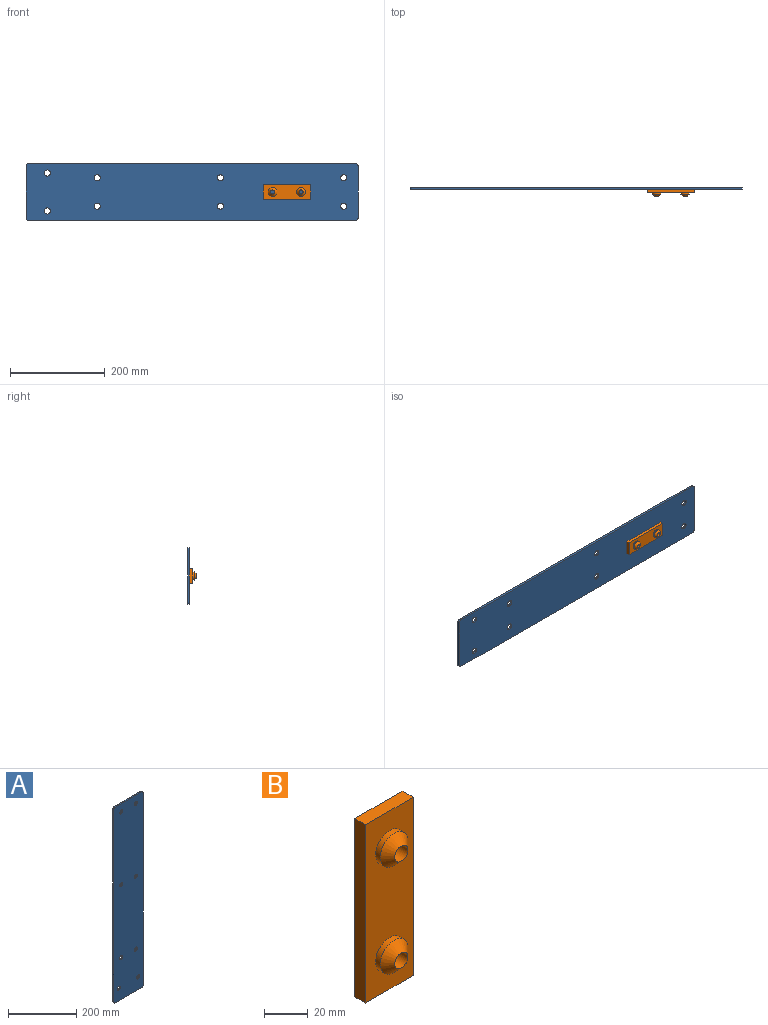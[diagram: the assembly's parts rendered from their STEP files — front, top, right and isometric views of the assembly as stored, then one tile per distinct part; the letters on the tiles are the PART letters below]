
ASSEMBLY  parts=2 mates=1
PART A: 18 faces, bbox 120x4x700 mm
  f0: plane 690x4mm, normal (-1,0,0), area 2760mm2, adj f12,f13,f14,f17
  f1: plane 110x4mm, normal (0,0,-1), area 440mm2, adj f12,f13,f14,f15
  f2: plane 690x4mm, normal (1,0,0), area 2760mm2, adj f12,f13,f15,f16
  f3: cylinder r=6.5mm len=13mm, axis (0,1,0), area 163.4mm2, adj f12,f13
  f4: cylinder r=6.5mm len=13mm, axis (0,1,0), area 163.4mm2, adj f12,f13
  f5: cylinder r=6.5mm len=13mm, axis (0,1,0), area 163.4mm2, adj f12,f13
  f6: cylinder r=6.5mm len=13mm, axis (0,1,0), area 163.4mm2, adj f12,f13
  f7: cylinder r=6.5mm len=13mm, axis (0,1,0), area 163.4mm2, adj f12,f13
  f8: cylinder r=6.5mm len=13mm, axis (0,1,0), area 163.4mm2, adj f12,f13
  f9: cylinder r=6.5mm len=13mm, axis (0,1,0), area 163.4mm2, adj f12,f13
  f10: plane 110x4mm, normal (0,0,1), area 440mm2, adj f12,f13,f16,f17
  f11: cylinder r=6.5mm len=13mm, axis (0,1,0), area 163.4mm2, adj f12,f13
  f12: plane 700x120mm, normal (0,-1,0), area 82916.7mm2, adj f0,f1,f2,f3,f4,f5,f6,f7
  f13: plane 700x120mm, normal (0,1,0), area 82916.7mm2, adj f0,f1,f2,f3,f4,f5,f6,f7
  f14: cylinder r=5mm len=5mm, axis (0,1,0), area 31.4mm2, adj f0,f1,f12,f13
  f15: cylinder r=5mm len=5mm, axis (0,1,0), area 31.4mm2, adj f1,f2,f12,f13
  f16: cylinder r=5mm len=5mm, axis (0,1,0), area 31.4mm2, adj f2,f10,f12,f13
  f17: cylinder r=5mm len=5mm, axis (0,1,0), area 31.4mm2, adj f0,f10,f12,f13
PART B: 16 faces, bbox 31x14.8x100 mm
  f0: cone r=9mm half-angle=45deg, axis (0,1,0), area 279.6mm2, adj f9,f12
  f1: cone r=4mm half-angle=45deg, axis (0,1,0), area 279.6mm2, adj f8,f10
  f2: plane 31x7mm, normal (0,0,1), area 217mm2, adj f3,f5,f6,f7
  f3: plane 100x7mm, normal (-1,0,0), area 700mm2, adj f2,f4,f6,f7
  f4: plane 31x7mm, normal (0,0,-1), area 217mm2, adj f3,f5,f6,f7
  f5: plane 100x7mm, normal (1,0,0), area 700mm2, adj f2,f4,f6,f7
  f6: plane 100x31mm, normal (0,-1,0), area 2591.1mm2, adj f2,f3,f4,f5,f8,f9
  f7: plane 100x31mm, normal (0,1,0), area 1933.6mm2, adj f2,f3,f4,f5,f14,f15
  f8: cylinder r=9mm len=18mm, axis (0,1,0), area 169.6mm2, adj f1,f6
  f9: cylinder r=9mm len=18mm, axis (0,1,0), area 169.6mm2, adj f0,f6
  f10: cylinder r=4.25mm len=10.75mm, axis (0,1,0), area 287.1mm2, adj f1,f11
  f11: plane 19.25x19.25mm, normal (0,1,0), area 234.3mm2, adj f10,f14
  f12: cylinder r=4.25mm len=10.75mm, axis (0,1,0), area 287.1mm2, adj f0,f13
  f13: plane 19.25x19.25mm, normal (0,1,0), area 234.3mm2, adj f12,f15
  f14: cone r=8.62mm half-angle=45deg, axis (0,1,0), area 413.2mm2, adj f7,f11
  f15: cone r=8.62mm half-angle=45deg, axis (0,1,0), area 413.2mm2, adj f7,f13
PLACE A rot(axis=(0.71,0,0.71),180deg) t=(-765.78,72.93,-66.05)mm fixed
PLACE B rot(axis=(0,-1,0),90deg) t=(-565.78,72.93,-66.05)mm
MATE slider B.f7 <-> A.f13  axis (0,1,0) through (-515.78,72.93,-66.05)mm
